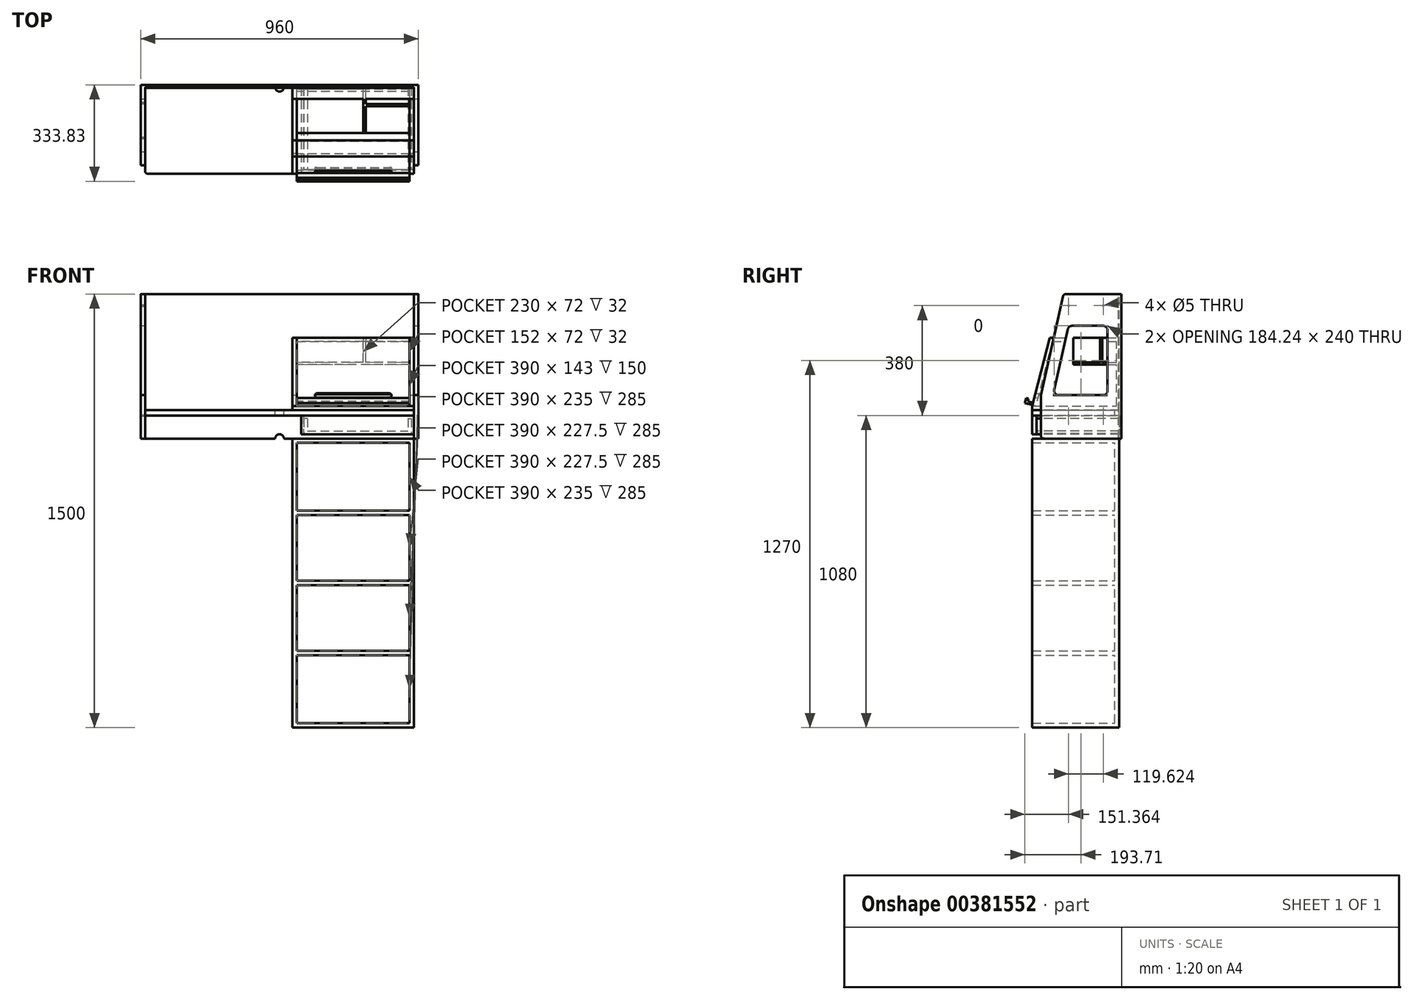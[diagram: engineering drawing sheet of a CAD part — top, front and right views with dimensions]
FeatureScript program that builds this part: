
annotation { "Feature Type Name" : "Feature", "Feature Type Description" : "" }
export const myFeature = defineFeature(function(context is Context, id is Id, definition is map)
    precondition{}
    {
        {
            var Q0;
            Q0=qCreatedBy(makeId("Front.planeOp"),FACE);
            var sketch = newSketch(context, id + "F0", { "sketchPlane" : qUnion([Q0])});
            skLineSegment(sketch, "E0.bottom", {"start": v(0, 0) * mm, "end": v(-960, 0) * mm});
            skLineSegment(sketch, "E0.top", {"start": v(0, 500) * mm, "end": v(-960, 500) * mm});
            skLineSegment(sketch, "E0.left", {"start": v(0, 0) * mm, "end": v(0, 500) * mm});
            skLineSegment(sketch, "E0.right", {"start": v(-960, 0) * mm, "end": v(-960, 500) * mm});
            skLineSegment(sketch, "E1.0", {"start": v(-945, 0) * mm, "end": v(-945, 500) * mm});
            skLineSegment(sketch, "E2.0", {"start": v(-15, 0) * mm, "end": v(-15, 500) * mm});
            skCircle(sketch, "E3", {"center": v(-480, 0) * mm, "radius": 15 * mm});
            skSolve(sketch);
        }
        {
            var Q0;
            {var subQ0=sQuery(id+"F0.wireOp",EDGE,"E0.right");Q0=makeQuery(id+"F0.imprint","IMPRINT",FACE,{"disambiguationData":[TD([[makeQuery(id+"F0.imprint","IMPRINT",EDGE,{"derivedFrom":subQ0}),-1.0]])]});}
            var Q1;
            {var subQ0=sQuery(id+"F0.wireOp",EDGE,"E1.0");Q1=makeQuery(id+"F0.imprint","IMPRINT",FACE,{"disambiguationData":[TD([[makeQuery(id+"F0.imprint","IMPRINT",EDGE,{"derivedFrom":subQ0}),-1.0]])]});}
            var Q2;
            {var subQ0=sQuery(id+"F0.wireOp",EDGE,"E0.left");Q2=makeQuery(id+"F0.imprint","IMPRINT",FACE,{"disambiguationData":[TD([[makeQuery(id+"F0.imprint","IMPRINT",EDGE,{"derivedFrom":subQ0}),1.0]])]});}
            extrude(context, id + "F1", {"entities" : qUnion([Q0, Q1, Q2]), "oppositeDirection" : true, "depth" : 8 * mm});
        }
        {
            var Q0;
            {var subQ0=sQuery(id+"F0.wireOp",EDGE,"E0.right");Q0=makeQuery(id+"F0.imprint","IMPRINT",FACE,{"disambiguationData":[TD([[makeQuery(id+"F0.imprint","IMPRINT",EDGE,{"derivedFrom":subQ0}),-1.0]])]});}
            var Q1;
            {var subQ0=sQuery(id+"F0.wireOp",EDGE,"E0.left");Q1=makeQuery(id+"F0.imprint","IMPRINT",FACE,{"disambiguationData":[TD([[makeQuery(id+"F0.imprint","IMPRINT",EDGE,{"derivedFrom":subQ0}),1.0]])]});}
            extrude(context, id + "F2", {"entities" : qUnion([Q0, Q1]), "operationType" : NewBodyOperationType.ADD, "depth" : 270 * mm});
        }
        {
            var Q0;
            {var subQ0=sQuery(id+"F0.wireOp",EDGE,"E0.top");Q0=makeQuery(id+"F2.opExtrude","CAP_EDGE",EDGE,{"disambiguationData":[OSD([subQ0]),TDD([makeQuery(id+"F0.imprint","IMPRINT",EDGE,{"disambiguationData":[TD([[makeQuery(id+"F0.imprint","INTERSECT",VERTEX,{"derivedFrom":[subQ0,sQuery(id+"F0.wireOp",EDGE,"E0.right")]}),1.0]])],"derivedFrom":subQ0})])],"isStart":false});}
            var Q1;
            {var subQ0=sQuery(id+"F0.wireOp",EDGE,"E0.top");Q1=makeQuery(id+"F2.opExtrude","CAP_EDGE",EDGE,{"disambiguationData":[OSD([subQ0]),TDD([makeQuery(id+"F0.imprint","IMPRINT",EDGE,{"disambiguationData":[TD([[makeQuery(id+"F0.imprint","INTERSECT",VERTEX,{"derivedFrom":[subQ0,sQuery(id+"F0.wireOp",EDGE,"E0.left")]}),-1.0]])],"derivedFrom":subQ0})])],"isStart":false});}
            chamfer(context, id + "F3", {"entities" : qUnion([Q0, Q1]), "chamferType" : ChamferType.TWO_OFFSETS, "width1" : 350 * mm, "oppositeDirection" : false, "width2" : 78 * mm, "tangentPropagation" : true});
        }
        {
            var Q0;
            Q0=makeQuery(id+"F2.opExtrude","SWEPT_FACE",FACE,{"disambiguationData":[OSD([sQuery(id+"F0.wireOp",EDGE,"E1.0")])]});
            var sketch = newSketch(context, id + "F4", { "sketchPlane" : qUnion([Q0])});
            skLineSegment(sketch, "E4.bottom", {"start": v(0, 80) * mm, "end": v(-270, 80) * mm});
            skLineSegment(sketch, "E4.top", {"start": v(0, 98) * mm, "end": v(-270, 98) * mm});
            skLineSegment(sketch, "E4.left", {"start": v(0, 80) * mm, "end": v(0, 98) * mm});
            skLineSegment(sketch, "E4.right", {"start": v(-270, 80) * mm, "end": v(-270, 98) * mm});
            skLineSegment(sketch, "E5", {"start": v(-174.47, 80) * mm, "end": v(-174.47, 500) * mm, "construction": true});
            skPoint(sketch, "E6", {"position": v(-174.47, 460) * mm});
            skPoint(sketch, "E7", {"position": v(-114.65, 98) * mm});
            skLineSegment(sketch, "E8", {"start": v(-114.65, 98) * mm, "end": v(-114.65, 164.65) * mm, "construction": true});
            skPoint(sketch, "E9.MirrorP", {"position": v(-54.84, 460) * mm});
            skPoint(sketch, "E10", {"position": v(-174.47, 80) * mm});
            skPoint(sketch, "E11.MirrorP", {"position": v(-54.84, 80) * mm});
            skLineSegment(sketch, "E12.bottom", {"start": v(-174.47, 390) * mm, "end": v(-40, 390) * mm});
            skLineSegment(sketch, "E12.top", {"start": v(-227.95, 150) * mm, "end": v(-40, 150) * mm});
            skLineSegment(sketch, "E12.left", {"start": v(-174.47, 390) * mm, "end": v(-227.95, 150) * mm});
            skLineSegment(sketch, "E12.right", {"start": v(-40, 390) * mm, "end": v(-40, 150) * mm});
            skLineSegment(sketch, "E13.bottom", {"start": v(-270, 98) * mm, "end": v(-300, 98) * mm});
            skLineSegment(sketch, "E13.top", {"start": v(-270, 80) * mm, "end": v(-300, 80) * mm});
            skLineSegment(sketch, "E13.left", {"start": v(-270, 98) * mm, "end": v(-270, 80) * mm});
            skLineSegment(sketch, "E13.right", {"start": v(-300, 98) * mm, "end": v(-300, 80) * mm});
            skSolve(sketch);
        }
        {
            var Q0;
            {var subQ0=sQuery(id+"F4.wireOp",EDGE,"E4.left");Q0=makeQuery(id+"F4.imprint","IMPRINT",FACE,{"disambiguationData":[TD([[makeQuery(id+"F4.imprint","IMPRINT",EDGE,{"derivedFrom":subQ0}),1.0]])]});}
            var Q1;
            {var subQ0=sQuery(id+"F4.wireOp",EDGE,"E4.right");Q1=makeQuery(id+"F4.imprint","IMPRINT",FACE,{"disambiguationData":[TD([[makeQuery(id+"F4.imprint","IMPRINT",EDGE,{"derivedFrom":subQ0}),-1.0]])]});}
            var Q2;
            Q2=makeQuery(id+"F4.imprint","IMPRINT",FACE,{"disambiguationData":[TD([[makeQuery(id+"F4.imprint","IMPRINT",EDGE,{"derivedFrom":sQuery(id+"F4.wireOp",EDGE,"E13.bottom")}),1.0]])]});
            var Q3;
            Q3=makeQuery(id+"F2.opExtrude","SWEPT_FACE",FACE,{"disambiguationData":[OSD([sQuery(id+"F0.wireOp",EDGE,"E2.0")])]});
            extrude(context, id + "F5", {"entities" : qUnion([Q0, Q1, Q2]), "endBound" : BoundingType.UP_TO_SURFACE, "endBoundEntityFace" : qUnion([Q3]), "depth" : 25 * mm});
        }
        {
            var Q0;
            Q0=makeQuery(id+"F5.opExtrude","CAP_EDGE",EDGE,{"disambiguationData":[OSD([sQuery(id+"F4.wireOp",EDGE,"E13.right")])],"isStart":true});
            var Q1;
            Q1=makeQuery(id+"F5.opExtrude","CAP_EDGE",EDGE,{"disambiguationData":[OSD([sQuery(id+"F4.wireOp",EDGE,"E13.right")])],"isStart":false});
            var Q2;
            {var subQ0=sQuery(id+"F0.wireOp",EDGE,"E0.top");var subQ1=makeQuery(id+"F0.imprint","IMPRINT",EDGE,{"disambiguationData":[TD([[makeQuery(id+"F0.imprint","INTERSECT",VERTEX,{"derivedFrom":[subQ0,sQuery(id+"F0.wireOp",EDGE,"E0.right")]}),1.0]])],"derivedFrom":subQ0});Q2=makeQuery(id+"F3.opChamfer","BLEND_EDGE",EDGE,{"blendedFrom":[makeQuery(id+"F2.opExtrude","CAP_EDGE",EDGE,{"disambiguationData":[OSD([subQ0]),TDD([subQ1])],"isStart":false}),makeQuery(id+"F2.boolean.opBoolean","MERGE",FACE,{"derivedFrom":[makeQuery(id+"F1.opExtrude","SWEPT_FACE",FACE,{"disambiguationData":[OSD([subQ0])]}),makeQuery(id+"F2.opExtrude","SWEPT_FACE",FACE,{"disambiguationData":[OSD([subQ0]),TDD([makeQuery(id+"F0.imprint","IMPRINT",EDGE,{"disambiguationData":[TD([[makeQuery(id+"F0.imprint","INTERSECT",VERTEX,{"derivedFrom":[subQ0,sQuery(id+"F0.wireOp",EDGE,"E0.left")]}),-1.0]])],"derivedFrom":subQ0})])]}),makeQuery(id+"F2.opExtrude","SWEPT_FACE",FACE,{"disambiguationData":[OSD([subQ0]),TDD([subQ1])]})]})],"blendedInto":[makeQuery(id+"F2.boolean.opBoolean","MERGE",FACE,{"derivedFrom":[makeQuery(id+"F1.opExtrude","SWEPT_FACE",FACE,{"disambiguationData":[OSD([subQ0])]}),makeQuery(id+"F2.opExtrude","SWEPT_FACE",FACE,{"disambiguationData":[OSD([subQ0]),TDD([makeQuery(id+"F0.imprint","IMPRINT",EDGE,{"disambiguationData":[TD([[makeQuery(id+"F0.imprint","INTERSECT",VERTEX,{"derivedFrom":[subQ0,sQuery(id+"F0.wireOp",EDGE,"E0.left")]}),-1.0]])],"derivedFrom":subQ0})])]}),makeQuery(id+"F2.opExtrude","SWEPT_FACE",FACE,{"disambiguationData":[OSD([subQ0]),TDD([subQ1])]})]})]});}
            var Q3;
            {var subQ0=sQuery(id+"F0.wireOp",EDGE,"E0.top");var subQ1=makeQuery(id+"F0.imprint","IMPRINT",EDGE,{"disambiguationData":[TD([[makeQuery(id+"F0.imprint","INTERSECT",VERTEX,{"derivedFrom":[subQ0,sQuery(id+"F0.wireOp",EDGE,"E0.left")]}),-1.0]])],"derivedFrom":subQ0});Q3=makeQuery(id+"F3.opChamfer","BLEND_EDGE",EDGE,{"blendedFrom":[makeQuery(id+"F2.opExtrude","CAP_EDGE",EDGE,{"disambiguationData":[OSD([subQ0]),TDD([subQ1])],"isStart":false}),makeQuery(id+"F2.boolean.opBoolean","MERGE",FACE,{"derivedFrom":[makeQuery(id+"F1.opExtrude","SWEPT_FACE",FACE,{"disambiguationData":[OSD([subQ0])]}),makeQuery(id+"F2.opExtrude","SWEPT_FACE",FACE,{"disambiguationData":[OSD([subQ0]),TDD([subQ1])]}),makeQuery(id+"F2.opExtrude","SWEPT_FACE",FACE,{"disambiguationData":[OSD([subQ0]),TDD([makeQuery(id+"F0.imprint","IMPRINT",EDGE,{"disambiguationData":[TD([[makeQuery(id+"F0.imprint","INTERSECT",VERTEX,{"derivedFrom":[subQ0,sQuery(id+"F0.wireOp",EDGE,"E0.right")]}),1.0]])],"derivedFrom":subQ0})])]})]})],"blendedInto":[makeQuery(id+"F2.boolean.opBoolean","MERGE",FACE,{"derivedFrom":[makeQuery(id+"F1.opExtrude","SWEPT_FACE",FACE,{"disambiguationData":[OSD([subQ0])]}),makeQuery(id+"F2.opExtrude","SWEPT_FACE",FACE,{"disambiguationData":[OSD([subQ0]),TDD([subQ1])]}),makeQuery(id+"F2.opExtrude","SWEPT_FACE",FACE,{"disambiguationData":[OSD([subQ0]),TDD([makeQuery(id+"F0.imprint","IMPRINT",EDGE,{"disambiguationData":[TD([[makeQuery(id+"F0.imprint","INTERSECT",VERTEX,{"derivedFrom":[subQ0,sQuery(id+"F0.wireOp",EDGE,"E0.right")]}),1.0]])],"derivedFrom":subQ0})])]})]})]});}
            var Q4;
            {var subQ0=sQuery(id+"F0.wireOp",EDGE,"E0.bottom");Q4=makeQuery(id+"F2.opExtrude","CAP_EDGE",EDGE,{"disambiguationData":[OSD([subQ0]),TDD([makeQuery(id+"F0.imprint","IMPRINT",EDGE,{"disambiguationData":[TD([[makeQuery(id+"F0.imprint","INTERSECT",VERTEX,{"derivedFrom":[subQ0,sQuery(id+"F0.wireOp",EDGE,"E0.left")]}),-1.0]])],"derivedFrom":subQ0})])],"isStart":false});}
            var Q5;
            {var subQ0=sQuery(id+"F0.wireOp",EDGE,"E0.bottom");Q5=makeQuery(id+"F2.opExtrude","CAP_EDGE",EDGE,{"disambiguationData":[OSD([subQ0]),TDD([makeQuery(id+"F0.imprint","IMPRINT",EDGE,{"disambiguationData":[TD([[makeQuery(id+"F0.imprint","INTERSECT",VERTEX,{"derivedFrom":[subQ0,sQuery(id+"F0.wireOp",EDGE,"E0.right")]}),1.0]])],"derivedFrom":subQ0})])],"isStart":false});}
            fillet(context, id + "F6", {"entities" : qUnion([Q0, Q1, Q2, Q3, Q4, Q5]), "radius" : 10 * mm, "tangentPropagation" : true, "allowEdgeOverflow" : false});
        }
        {
            var Q0;
            Q0=qCreatedBy(makeId("Front.planeOp"),FACE);
            var sketch = newSketch(context, id + "F7", { "sketchPlane" : qUnion([Q0])});
            skLineSegment(sketch, "E14.bottom", {"start": v(-15, 98) * mm, "end": v(-435, 98) * mm});
            skLineSegment(sketch, "E14.top", {"start": v(-15, 348) * mm, "end": v(-435, 348) * mm});
            skLineSegment(sketch, "E14.left", {"start": v(-15, 98) * mm, "end": v(-15, 348) * mm});
            skLineSegment(sketch, "E14.right", {"start": v(-435, 98) * mm, "end": v(-435, 348) * mm});
            skLineSegment(sketch, "E15.0", {"start": v(-420, 95) * mm, "end": v(-420, 348) * mm});
            skLineSegment(sketch, "E16.0", {"start": v(-30, 98) * mm, "end": v(-30, 348) * mm});
            skLineSegment(sketch, "E17.0", {"start": v(-15, 113) * mm, "end": v(-435, 113) * mm});
            skSolve(sketch);
        }
        {
            var Q0;
            {var subQ0=sQuery(id+"F7.wireOp",EDGE,"E14.right");var subQ1=sQuery(id+"F7.wireOp",EDGE,"E14.top");var subQ2=makeQuery(id+"F7.imprint","INTERSECT",VERTEX,{"derivedFrom":[subQ1,subQ0]});Q0=makeQuery(id+"F7.imprint","IMPRINT",FACE,{"disambiguationData":[TD([[makeQuery(id+"F7.imprint","IMPRINT",EDGE,{"disambiguationData":[TD([[subQ2,1.0]])],"derivedFrom":subQ1}),1.0]])]});}
            var Q1;
            {var subQ0=sQuery(id+"F7.wireOp",EDGE,"E14.right");var subQ1=sQuery(id+"F7.wireOp",EDGE,"E14.bottom");var subQ2=makeQuery(id+"F7.imprint","INTERSECT",VERTEX,{"derivedFrom":[subQ1,subQ0]});Q1=makeQuery(id+"F7.imprint","IMPRINT",FACE,{"disambiguationData":[TD([[makeQuery(id+"F7.imprint","IMPRINT",EDGE,{"disambiguationData":[TD([[subQ2,1.0]])],"derivedFrom":subQ1}),-1.0]])]});}
            var Q2;
            {var subQ0=sQuery(id+"F7.wireOp",EDGE,"E14.left");var subQ1=sQuery(id+"F7.wireOp",EDGE,"E14.top");var subQ2=makeQuery(id+"F7.imprint","INTERSECT",VERTEX,{"derivedFrom":[subQ1,subQ0]});Q2=makeQuery(id+"F7.imprint","IMPRINT",FACE,{"disambiguationData":[TD([[makeQuery(id+"F7.imprint","IMPRINT",EDGE,{"disambiguationData":[TD([[subQ2,-1.0]])],"derivedFrom":subQ1}),1.0]])]});}
            var Q3;
            {var subQ0=sQuery(id+"F7.wireOp",EDGE,"E14.left");var subQ1=sQuery(id+"F7.wireOp",EDGE,"E14.bottom");var subQ2=makeQuery(id+"F7.imprint","INTERSECT",VERTEX,{"derivedFrom":[subQ1,subQ0]});Q3=makeQuery(id+"F7.imprint","IMPRINT",FACE,{"disambiguationData":[TD([[makeQuery(id+"F7.imprint","IMPRINT",EDGE,{"disambiguationData":[TD([[subQ2,-1.0]])],"derivedFrom":subQ1}),-1.0]])]});}
            var Q4;
            {var subQ0=sQuery(id+"F7.wireOp",EDGE,"E15.0");var subQ1=sQuery(id+"F7.wireOp",EDGE,"E14.bottom");var subQ2=makeQuery(id+"F7.imprint","INTERSECT",VERTEX,{"derivedFrom":[subQ1,subQ0]});Q4=makeQuery(id+"F7.imprint","IMPRINT",FACE,{"disambiguationData":[TD([[makeQuery(id+"F7.imprint","IMPRINT",EDGE,{"disambiguationData":[TD([[subQ2,1.0]])],"derivedFrom":subQ1}),-1.0]])]});}
            extrude(context, id + "F8", {"entities" : qUnion([Q0, Q1, Q2, Q3, Q4]), "depth" : 300 * mm});
        }
        {
            var Q0;
            {var subQ0=sQuery(id+"F7.wireOp",EDGE,"E15.0");var subQ1=sQuery(id+"F7.wireOp",EDGE,"E14.top");var subQ2=makeQuery(id+"F7.imprint","INTERSECT",VERTEX,{"derivedFrom":[subQ1,subQ0]});Q0=makeQuery(id+"F7.imprint","IMPRINT",FACE,{"disambiguationData":[TD([[makeQuery(id+"F7.imprint","IMPRINT",EDGE,{"disambiguationData":[TD([[subQ2,1.0]])],"derivedFrom":subQ1}),1.0]])]});}
            extrude(context, id + "F9", {"entities" : qUnion([Q0]), "depth" : 8 * mm});
        }
        {
            var Q0;
            {var subQ0=sQuery(id+"F7.wireOp",EDGE,"E14.top");Q0=makeQuery(id+"F8.opExtrude","CAP_EDGE",EDGE,{"disambiguationData":[OSD([subQ0]),TDD([makeQuery(id+"F7.imprint","IMPRINT",EDGE,{"disambiguationData":[TD([[makeQuery(id+"F7.imprint","INTERSECT",VERTEX,{"derivedFrom":[subQ0,sQuery(id+"F7.wireOp",EDGE,"E14.right")]}),1.0]])],"derivedFrom":subQ0})])],"isStart":false});}
            var Q1;
            {var subQ0=sQuery(id+"F7.wireOp",EDGE,"E14.top");Q1=makeQuery(id+"F8.opExtrude","CAP_EDGE",EDGE,{"disambiguationData":[OSD([subQ0]),TDD([makeQuery(id+"F7.imprint","IMPRINT",EDGE,{"disambiguationData":[TD([[makeQuery(id+"F7.imprint","INTERSECT",VERTEX,{"derivedFrom":[subQ0,sQuery(id+"F7.wireOp",EDGE,"E14.left")]}),-1.0]])],"derivedFrom":subQ0})])],"isStart":false});}
            chamfer(context, id + "F10", {"entities" : qUnion([Q0, Q1]), "chamferType" : ChamferType.TWO_OFFSETS, "width1" : 235 * mm, "oppositeDirection" : false, "width2" : 60 * mm, "tangentPropagation" : true});
        }
        {
            var Q0;
            Q0=makeQuery(id+"F8.opExtrude","SWEPT_FACE",FACE,{"disambiguationData":[OSD([sQuery(id+"F7.wireOp",EDGE,"E15.0")])]});
            var sketch = newSketch(context, id + "F11", { "sketchPlane" : qUnion([Q0])});
            skLineSegment(sketch, "E18", {"start": v(-240, 348) * mm, "end": v(-299.24, 115.97) * mm});
            skLineSegment(sketch, "E19", {"start": v(-299.24, 115.97) * mm, "end": v(-287.62, 113) * mm});
            skLineSegment(sketch, "E20", {"start": v(-287.62, 113) * mm, "end": v(-227.62, 348) * mm});
            skLineSegment(sketch, "E21", {"start": v(-227.62, 348) * mm, "end": v(-240, 348) * mm});
            skLineSegment(sketch, "E22.0", {"start": v(-243.06, 336) * mm, "end": v(0, 336) * mm});
            skLineSegment(sketch, "E23", {"start": v(-299.24, 115.97) * mm, "end": v(-325.83, 122.76) * mm});
            skLineSegment(sketch, "E24", {"start": v(-325.83, 122.76) * mm, "end": v(-321.38, 140.2) * mm});
            skLineSegment(sketch, "E25", {"start": v(-321.38, 140.2) * mm, "end": v(-313.63, 138.22) * mm});
            skLineSegment(sketch, "E26", {"start": v(-313.63, 138.22) * mm, "end": v(-316.1, 128.53) * mm});
            skLineSegment(sketch, "E27", {"start": v(-316.1, 128.53) * mm, "end": v(-297.26, 123.72) * mm});
            skPoint(sketch, "E28", {"position": v(-158, 336) * mm});
            skPoint(sketch, "E28.positionSnap0", {"position": v(-158, 348) * mm});
            skLineSegment(sketch, "E29", {"start": v(-158, 348) * mm, "end": v(-158, 336) * mm});
            skLineSegment(sketch, "E30.bottom", {"start": v(-158, 256) * mm, "end": v(-8, 256) * mm});
            skLineSegment(sketch, "E30.top", {"start": v(-158, 264) * mm, "end": v(-8, 264) * mm});
            skLineSegment(sketch, "E30.left", {"start": v(-158, 264) * mm, "end": v(-158, 256) * mm});
            skLineSegment(sketch, "E30.right", {"start": v(-8, 264) * mm, "end": v(-8, 256) * mm});
            skSolve(sketch);
        }
        {
            var Q0;
            {var subQ1=sQuery(id+"F7.wireOp",EDGE,"E15.0");var subQ4=sQuery(id+"F11.wireOp",EDGE,"E22.0");var subQ6=makeQuery(id+"F8.opExtrude","CAP_EDGE",EDGE,{"disambiguationData":[OSD([subQ1])],"isStart":true});var subQ8=makeQuery(id+"F11.imprint","INTERSECT",VERTEX,{"derivedFrom":[subQ6,subQ4]});Q0=makeQuery(id+"F11.imprint","IMPRINT",FACE,{"disambiguationData":[TD([[makeQuery(id+"F11.imprint","IMPRINT",EDGE,{"disambiguationData":[TD([[subQ8,1.0]])],"derivedFrom":subQ4}),1.0]])]});}
            var Q1;
            {var subQ0=sQuery(id+"F11.wireOp",EDGE,"E21");Q1=makeQuery(id+"F11.imprint","IMPRINT",FACE,{"disambiguationData":[TD([[makeQuery(id+"F11.imprint","IMPRINT",EDGE,{"derivedFrom":subQ0}),-1.0]])]});}
            var Q2;
            {var subQ0=sQuery(id+"F11.wireOp",EDGE,"E19");Q2=makeQuery(id+"F11.imprint","IMPRINT",FACE,{"disambiguationData":[TD([[makeQuery(id+"F11.imprint","IMPRINT",EDGE,{"derivedFrom":subQ0}),1.0]])]});}
            var Q3;
            {var subQ0=sQuery(id+"F11.wireOp",EDGE,"E23");Q3=makeQuery(id+"F11.imprint","IMPRINT",FACE,{"disambiguationData":[TD([[makeQuery(id+"F11.imprint","IMPRINT",EDGE,{"derivedFrom":subQ0}),-1.0]])]});}
            var Q4;
            {var subQ5=sQuery(id+"F11.wireOp",EDGE,"Vka6C3qe-eKzw-OUEN-JvXl-aBNwLwRMFBuR");Q4=makeQuery(id+"F11.imprint","IMPRINT",FACE,{"disambiguationData":[TD([[makeQuery(id+"F11.imprint","IMPRINT",EDGE,{"derivedFrom":subQ5}),-1.0]])]});}
            var Q5;
            {var subQ5=sQuery(id+"F11.wireOp",EDGE,"E29");Q5=makeQuery(id+"F11.imprint","IMPRINT",FACE,{"disambiguationData":[TD([[makeQuery(id+"F11.imprint","IMPRINT",EDGE,{"derivedFrom":subQ5}),-1.0]])]});}
            var Q6;
            Q6=makeQuery(id+"F8.opExtrude","SWEPT_FACE",FACE,{"disambiguationData":[OSD([sQuery(id+"F7.wireOp",EDGE,"E16.0")])]});
            extrude(context, id + "F12", {"entities" : qUnion([Q0, Q1, Q2, Q3, Q4, Q5]), "endBound" : BoundingType.UP_TO_SURFACE, "endBoundEntityFace" : qUnion([Q6]), "depth" : 25 * mm});
        }
        {
            var Q0;
            Q0=makeQuery(id+"F12.opExtrude","SWEPT_FACE",FACE,{"disambiguationData":[OSD([sQuery(id+"F11.wireOp",EDGE,"E18")])]});
            var sketch = newSketch(context, id + "F13", { "sketchPlane" : qUnion([Q0])});
            skLineSegment(sketch, "E31.bottom", {"start": v(-350, 80.12) * mm, "end": v(-100, 80.12) * mm});
            skLineSegment(sketch, "E31.top", {"start": v(-350, 65.12) * mm, "end": v(-100, 65.12) * mm});
            skLineSegment(sketch, "E31.left", {"start": v(-350, 80.12) * mm, "end": v(-350, 65.12) * mm});
            skLineSegment(sketch, "E31.right", {"start": v(-100, 80.12) * mm, "end": v(-100, 65.12) * mm});
            skPoint(sketch, "E32", {"position": v(-225, 80.12) * mm});
            skArc(sketch, "E33", {"start": v(-350, 80.12) * mm, "mid": v(-357.5, 72.62) * mm, "end": v(-350, 65.12) * mm});
            skArc(sketch, "E34", {"start": v(-100, 65.12) * mm, "mid": v(-92.5, 72.62) * mm, "end": v(-100, 80.12) * mm});
            skSolve(sketch);
        }
        {
            var Q0;
            Q0=makeQuery(id+"F13.imprint","IMPRINT",FACE,{"disambiguationData":[TD([[makeQuery(id+"F13.imprint","IMPRINT",EDGE,{"derivedFrom":sQuery(id+"F13.wireOp",EDGE,"E31.bottom")}),-1.0]])]});
            var Q1;
            Q1=makeQuery(id+"F13.imprint","IMPRINT",FACE,{"disambiguationData":[TD([[makeQuery(id+"F13.imprint","IMPRINT",EDGE,{"derivedFrom":sQuery(id+"F13.wireOp",EDGE,"E31.left")}),-1.0]])]});
            var Q2;
            Q2=makeQuery(id+"F13.imprint","IMPRINT",FACE,{"disambiguationData":[TD([[makeQuery(id+"F13.imprint","IMPRINT",EDGE,{"derivedFrom":sQuery(id+"F13.wireOp",EDGE,"E31.right")}),1.0]])]});
            extrude(context, id + "F14", {"entities" : qUnion([Q0, Q1, Q2]), "operationType" : NewBodyOperationType.REMOVE, "oppositeDirection" : true, "depth" : 25 * mm});
        }
        {
            var Q0;
            {var subQ4=sQuery(id+"F11.wireOp",EDGE,"E29");Q0=makeQuery(id+"F11.imprint","IMPRINT",FACE,{"disambiguationData":[TD([[makeQuery(id+"F11.imprint","IMPRINT",EDGE,{"derivedFrom":subQ4}),1.0]])]});}
            var Q1;
            Q1=makeQuery(id+"F8.opExtrude","SWEPT_FACE",FACE,{"disambiguationData":[OSD([sQuery(id+"F7.wireOp",EDGE,"E16.0")])]});
            extrude(context, id + "F15", {"entities" : qUnion([Q0]), "endBound" : BoundingType.UP_TO_SURFACE, "endBoundEntityFace" : qUnion([Q1]), "depth" : 25 * mm});
        }
        {
            var Q0;
            Q0=makeQuery(id+"F15.opExtrude","SWEPT_BODY",BODY,{"disambiguationData":[OSD([sQuery(id+"F7.wireOp",EDGE,"E14.top"),sQuery(id+"F7.wireOp",EDGE,"E15.0"),sQuery(id+"F11.wireOp",EDGE,"E22.0"),sQuery(id+"F11.wireOp",EDGE,"E29")])]});
            var Q1;
            Q1=makeQuery(id+"F12.opExtrude","SWEPT_BODY",BODY,{"disambiguationData":[OSD([sQuery(id+"F7.wireOp",EDGE,"E14.top"),sQuery(id+"F7.wireOp",EDGE,"E15.0"),sQuery(id+"F11.wireOp",EDGE,"E18"),sQuery(id+"F11.wireOp",EDGE,"E19"),sQuery(id+"F11.wireOp",EDGE,"E20"),sQuery(id+"F11.wireOp",EDGE,"E21"),sQuery(id+"F11.wireOp",EDGE,"E22.0"),sQuery(id+"F11.wireOp",EDGE,"E23"),sQuery(id+"F11.wireOp",EDGE,"E24"),sQuery(id+"F11.wireOp",EDGE,"E25"),sQuery(id+"F11.wireOp",EDGE,"E26"),sQuery(id+"F11.wireOp",EDGE,"E27")])]});
            booleanBodies(context, id + "F16", {"operationType" : BooleanOperationType.SUBTRACTION, "tools" : qUnion([Q0]), "targets" : qUnion([Q1]), "keepTools" : true});
        }
        {
            var Q0;
            Q0=makeQuery(id+"F5.opExtrude","SWEPT_FACE",FACE,{"disambiguationData":[OSD([sQuery(id+"F4.wireOp",EDGE,"E13.right")])]});
            var sketch = newSketch(context, id + "F17", { "sketchPlane" : qUnion([Q0])});
            skLineSegment(sketch, "E35.bottom", {"start": v(-15, 80) * mm, "end": v(-405, 80) * mm});
            skLineSegment(sketch, "E35.top", {"start": v(-15, 15) * mm, "end": v(-405, 15) * mm});
            skLineSegment(sketch, "E35.left", {"start": v(-15, 80) * mm, "end": v(-15, 15) * mm});
            skLineSegment(sketch, "E35.right", {"start": v(-405, 80) * mm, "end": v(-405, 15) * mm});
            skLineSegment(sketch, "E36.bottom", {"start": v(-405, 15) * mm, "end": v(-420, 15) * mm});
            skLineSegment(sketch, "E36.top", {"start": v(-405, 80) * mm, "end": v(-420, 80) * mm});
            skLineSegment(sketch, "E36.left", {"start": v(-405, 15) * mm, "end": v(-405, 80) * mm});
            skLineSegment(sketch, "E36.right", {"start": v(-420, 15) * mm, "end": v(-420, 80) * mm});
            skSolve(sketch);
        }
        {
            var Q0;
            Q0=makeQuery(id+"F17.imprint","IMPRINT",FACE,{"disambiguationData":[TD([[makeQuery(id+"F17.imprint","IMPRINT",EDGE,{"derivedFrom":sQuery(id+"F17.wireOp",EDGE,"E35.bottom")}),1.0]])]});
            extrude(context, id + "F18", {"entities" : qUnion([Q0]), "oppositeDirection" : true, "depth" : 15 * mm});
        }
        {
            var Q0;
            Q0=makeQuery(id+"F18.opExtrude","CAP_FACE",FACE,{"disambiguationData":[OSD([sQuery(id+"F17.wireOp",EDGE,"E35.bottom"),sQuery(id+"F17.wireOp",EDGE,"E35.top"),sQuery(id+"F17.wireOp",EDGE,"E35.left"),sQuery(id+"F17.wireOp",EDGE,"E35.right")])],"isStart":false});
            var sketch = newSketch(context, id + "F19", { "sketchPlane" : qUnion([Q0])});
            skLineSegment(sketch, "E37.bottom", {"start": v(24, 15) * mm, "end": v(36, 15) * mm});
            skLineSegment(sketch, "E37.top", {"start": v(24, 68.96) * mm, "end": v(36, 68.96) * mm});
            skLineSegment(sketch, "E37.left", {"start": v(24, 15) * mm, "end": v(24, 68.96) * mm});
            skLineSegment(sketch, "E37.right", {"start": v(36, 15) * mm, "end": v(36, 68.96) * mm});
            skLineSegment(sketch, "E38.bottom", {"start": v(396, 15) * mm, "end": v(384, 15) * mm});
            skLineSegment(sketch, "E38.top", {"start": v(396, 68.96) * mm, "end": v(384, 68.96) * mm});
            skLineSegment(sketch, "E38.left", {"start": v(396, 15) * mm, "end": v(396, 68.96) * mm});
            skLineSegment(sketch, "E38.right", {"start": v(384, 15) * mm, "end": v(384, 68.96) * mm});
            skLineSegment(sketch, "E39.bottom", {"start": v(36, 25.56) * mm, "end": v(384, 25.56) * mm});
            skLineSegment(sketch, "E39.top", {"start": v(36, 17.56) * mm, "end": v(384, 17.56) * mm});
            skLineSegment(sketch, "E39.left", {"start": v(36, 25.56) * mm, "end": v(36, 17.56) * mm});
            skLineSegment(sketch, "E39.right", {"start": v(384, 25.56) * mm, "end": v(384, 17.56) * mm});
            skLineSegment(sketch, "E40.bottom", {"start": v(405, 15) * mm, "end": v(397, 15) * mm});
            skLineSegment(sketch, "E40.top", {"start": v(405, 80) * mm, "end": v(397, 80) * mm});
            skLineSegment(sketch, "E40.left", {"start": v(405, 15) * mm, "end": v(405, 80) * mm});
            skLineSegment(sketch, "E40.right", {"start": v(397, 15) * mm, "end": v(397, 80) * mm});
            skSolve(sketch);
        }
        {
            var Q0;
            {var subQ1=sQuery(id+"F19.wireOp",EDGE,"E37.bottom");Q0=makeQuery(id+"F19.imprint","IMPRINT",FACE,{"disambiguationData":[TD([[makeQuery(id+"F19.imprint","IMPRINT",EDGE,{"derivedFrom":subQ1}),1.0]])]});}
            var Q1;
            Q1=makeQuery(id+"F19.imprint","IMPRINT",FACE,{"disambiguationData":[TD([[makeQuery(id+"F19.imprint","IMPRINT",EDGE,{"derivedFrom":sQuery(id+"F19.wireOp",EDGE,"E39.bottom")}),-1.0]])]});
            var Q2;
            {var subQ1=sQuery(id+"F19.wireOp",EDGE,"E38.bottom");Q2=makeQuery(id+"F19.imprint","IMPRINT",FACE,{"disambiguationData":[TD([[makeQuery(id+"F19.imprint","IMPRINT",EDGE,{"derivedFrom":subQ1}),1.0]])]});}
            var Q3;
            Q3=makeQuery(id+"F5.opExtrude","SWEPT_FACE",FACE,{"disambiguationData":[OSD([sQuery(id+"F4.wireOp",EDGE,"E4.left")])]});
            extrude(context, id + "F20", {"entities" : qUnion([Q0, Q1, Q2]), "endBound" : BoundingType.UP_TO_SURFACE, "endBoundEntityFace" : qUnion([Q3]), "depth" : 25 * mm});
        }
        {
            var Q0;
            Q0=makeQuery(id+"F19.imprint","IMPRINT",FACE,{"disambiguationData":[TD([[makeQuery(id+"F19.imprint","IMPRINT",EDGE,{"derivedFrom":sQuery(id+"F19.wireOp",EDGE,"E40.bottom")}),1.0]])]});
            var Q1;
            Q1=makeQuery(id+"F1.opExtrude","CAP_FACE",FACE,{"disambiguationData":[OSD([sQuery(id+"F0.wireOp",EDGE,"E0.bottom"),sQuery(id+"F0.wireOp",EDGE,"E0.top"),sQuery(id+"F0.wireOp",EDGE,"E0.left"),sQuery(id+"F0.wireOp",EDGE,"E0.right"),sQuery(id+"F0.wireOp",EDGE,"E3")])],"isStart":true});
            extrude(context, id + "F21", {"entities" : qUnion([Q0]), "endBound" : BoundingType.UP_TO_SURFACE, "endBoundEntityFace" : qUnion([Q1]), "depth" : 25 * mm});
        }
        {
            var Q0;
            Q0=sQuery(id+"F4.wireOp",VERTEX,"E6");
            var Q1;
            Q1=sQuery(id+"F4.wireOp",VERTEX,"E9.MirrorP");
            var Q2;
            Q2=sQuery(id+"F4.wireOp",VERTEX,"E10");
            var Q3;
            Q3=sQuery(id+"F4.wireOp",VERTEX,"E11.MirrorP");
            var Q4;
            Q4=makeQuery(id+"F1.opExtrude","SWEPT_BODY",BODY,{"disambiguationData":[OSD([sQuery(id+"F0.wireOp",EDGE,"E0.bottom"),sQuery(id+"F0.wireOp",EDGE,"E0.top"),sQuery(id+"F0.wireOp",EDGE,"E0.left"),sQuery(id+"F0.wireOp",EDGE,"E0.right"),sQuery(id+"F0.wireOp",EDGE,"E3")])]});
            hole(context, id + "F22", {"style" : HoleStyle.SIMPLE, "endStyle" : HoleEndStyle.BLIND, "holeDiameter" : 5 * mm, "holeDepth" : 12 * mm, "isTappedThrough" : true, "tappedDepth" : 12 * mm, "tapClearance" : 3, "locations" : qUnion([Q0, Q1, Q2, Q3]), "scope" : qUnion([Q4])});
        }
        {
            var Q0;
            Q0=makeQuery(id+"F4.imprint","IMPRINT",FACE,{"disambiguationData":[TD([[makeQuery(id+"F4.imprint","IMPRINT",EDGE,{"derivedFrom":sQuery(id+"F4.wireOp",EDGE,"E12.bottom")}),-1.0]])]});
            var Q1;
            {var subQ0=sQuery(id+"F0.wireOp",EDGE,"E0.left");Q1=makeQuery(id+"F2.boolean.opBoolean","MERGE",FACE,{"derivedFrom":[makeQuery(id+"F1.opExtrude","SWEPT_FACE",FACE,{"disambiguationData":[OSD([subQ0])]}),makeQuery(id+"F2.opExtrude","SWEPT_FACE",FACE,{"disambiguationData":[OSD([subQ0])]})]});}
            extrude(context, id + "F23", {"entities" : qUnion([Q0]), "operationType" : NewBodyOperationType.REMOVE, "oppositeDirection" : true, "depth" : 25 * mm, "hasSecondDirection" : true, "secondDirectionBound" : SecondDirectionBoundingType.UP_TO_SURFACE, "secondDirectionOppositeDirection" : false, "secondDirectionBoundEntityFace" : qUnion([Q1]), "secondDirectionDepth" : 25 * mm});
        }
        {
            var Q0;
            {var subQ0=sQuery(id+"F4.wireOp",EDGE,"E12.top");var subQ1=sQuery(id+"F0.wireOp",EDGE,"E0.right");var subQ2=sQuery(id+"F4.wireOp",EDGE,"E12.right");Q0=makeQuery(id+"F23.boolean.opBoolean","COPY",EDGE,{"disambiguationData":[TD([makeQuery(id+"F1.opExtrude","SWEPT_FACE",FACE,{"disambiguationData":[OSD([subQ1])]})])],"derivedFrom":makeQuery(id+"F23.opExtrude","SWEPT_EDGE",EDGE,{"disambiguationData":[OSD([subQ0,subQ2])]})});}
            var Q1;
            {var subQ0=sQuery(id+"F4.wireOp",EDGE,"E12.top");var subQ1=sQuery(id+"F0.wireOp",EDGE,"E0.right");var subQ2=sQuery(id+"F4.wireOp",EDGE,"E12.left");Q1=makeQuery(id+"F23.boolean.opBoolean","COPY",EDGE,{"disambiguationData":[TD([makeQuery(id+"F1.opExtrude","SWEPT_FACE",FACE,{"disambiguationData":[OSD([subQ1])]})])],"derivedFrom":makeQuery(id+"F23.opExtrude","SWEPT_EDGE",EDGE,{"disambiguationData":[OSD([subQ0,subQ2])]})});}
            var Q2;
            {var subQ0=sQuery(id+"F4.wireOp",EDGE,"E12.bottom");var subQ1=sQuery(id+"F0.wireOp",EDGE,"E0.right");var subQ2=sQuery(id+"F4.wireOp",EDGE,"E12.right");Q2=makeQuery(id+"F23.boolean.opBoolean","COPY",EDGE,{"disambiguationData":[TD([makeQuery(id+"F1.opExtrude","SWEPT_FACE",FACE,{"disambiguationData":[OSD([subQ1])]})])],"derivedFrom":makeQuery(id+"F23.opExtrude","SWEPT_EDGE",EDGE,{"disambiguationData":[OSD([subQ0,subQ2])]})});}
            var Q3;
            {var subQ0=sQuery(id+"F4.wireOp",EDGE,"E12.top");var subQ1=sQuery(id+"F0.wireOp",EDGE,"E0.left");var subQ2=sQuery(id+"F4.wireOp",EDGE,"E12.left");Q3=makeQuery(id+"F23.boolean.opBoolean","COPY",EDGE,{"disambiguationData":[TD([makeQuery(id+"F1.opExtrude","SWEPT_FACE",FACE,{"disambiguationData":[OSD([subQ1])]})])],"derivedFrom":makeQuery(id+"F23.opExtrude","SWEPT_EDGE",EDGE,{"disambiguationData":[OSD([subQ0,subQ2])]})});}
            var Q4;
            {var subQ0=sQuery(id+"F4.wireOp",EDGE,"E12.top");var subQ1=sQuery(id+"F0.wireOp",EDGE,"E0.left");var subQ2=sQuery(id+"F4.wireOp",EDGE,"E12.right");Q4=makeQuery(id+"F23.boolean.opBoolean","COPY",EDGE,{"disambiguationData":[TD([makeQuery(id+"F1.opExtrude","SWEPT_FACE",FACE,{"disambiguationData":[OSD([subQ1])]})])],"derivedFrom":makeQuery(id+"F23.opExtrude","SWEPT_EDGE",EDGE,{"disambiguationData":[OSD([subQ0,subQ2])]})});}
            var Q5;
            {var subQ0=sQuery(id+"F0.wireOp",EDGE,"E0.left");var subQ1=sQuery(id+"F4.wireOp",EDGE,"E12.bottom");var subQ2=sQuery(id+"F4.wireOp",EDGE,"E12.right");Q5=makeQuery(id+"F23.boolean.opBoolean","COPY",EDGE,{"disambiguationData":[TD([makeQuery(id+"F1.opExtrude","SWEPT_FACE",FACE,{"disambiguationData":[OSD([subQ0])]})])],"derivedFrom":makeQuery(id+"F23.opExtrude","SWEPT_EDGE",EDGE,{"disambiguationData":[OSD([subQ1,subQ2])]})});}
            var Q6;
            {var subQ0=sQuery(id+"F0.wireOp",EDGE,"E0.left");var subQ1=sQuery(id+"F4.wireOp",EDGE,"E12.bottom");var subQ2=sQuery(id+"F4.wireOp",EDGE,"E12.left");Q6=makeQuery(id+"F23.boolean.opBoolean","COPY",EDGE,{"disambiguationData":[TD([makeQuery(id+"F1.opExtrude","SWEPT_FACE",FACE,{"disambiguationData":[OSD([subQ0])]})])],"derivedFrom":makeQuery(id+"F23.opExtrude","SWEPT_EDGE",EDGE,{"disambiguationData":[OSD([subQ1,subQ2])]})});}
            var Q7;
            {var subQ0=sQuery(id+"F4.wireOp",EDGE,"E12.bottom");var subQ1=sQuery(id+"F0.wireOp",EDGE,"E0.right");var subQ2=sQuery(id+"F4.wireOp",EDGE,"E12.left");Q7=makeQuery(id+"F23.boolean.opBoolean","COPY",EDGE,{"disambiguationData":[TD([makeQuery(id+"F1.opExtrude","SWEPT_FACE",FACE,{"disambiguationData":[OSD([subQ1])]})])],"derivedFrom":makeQuery(id+"F23.opExtrude","SWEPT_EDGE",EDGE,{"disambiguationData":[OSD([subQ0,subQ2])]})});}
            fillet(context, id + "F24", {"entities" : qUnion([Q0, Q1, Q2, Q3, Q4, Q5, Q6, Q7]), "radius" : 15 * mm, "tangentPropagation" : true, "allowEdgeOverflow" : false});
        }
        {
            var Q0;
            Q0=makeQuery(id+"F5.opExtrude","SWEPT_FACE",FACE,{"disambiguationData":[OSD([sQuery(id+"F4.wireOp",EDGE,"E4.top"),sQuery(id+"F4.wireOp",EDGE,"E13.bottom")])]});
            var sketch = newSketch(context, id + "F25", { "sketchPlane" : qUnion([Q0])});
            skCircle(sketch, "E41", {"center": v(-480, 0) * mm, "radius": 15 * mm});
            skSolve(sketch);
        }
        {
            var Q0;
            {var subQ0=sQuery(id+"F25.wireOp",EDGE,"E41");var subQ1=makeQuery(id+"F5.opExtrude","SWEPT_EDGE",EDGE,{"disambiguationData":[OSD([sQuery(id+"F0.wireOp",EDGE,"E1.0"),sQuery(id+"F4.wireOp",EDGE,"E4.top"),sQuery(id+"F4.wireOp",EDGE,"E4.left")])]});var subQ2=makeQuery(id+"F25.imprint","INTERSECT",VERTEX,{"disambiguationData":[OD(0.0)],"derivedFrom":[subQ1,subQ0]});Q0=makeQuery(id+"F25.imprint","IMPRINT",FACE,{"disambiguationData":[TD([[makeQuery(id+"F25.imprint","IMPRINT",EDGE,{"disambiguationData":[TD([[subQ2,-1.0]])],"derivedFrom":subQ0}),1.0]])]});}
            extrude(context, id + "F26", {"entities" : qUnion([Q0]), "operationType" : NewBodyOperationType.REMOVE, "oppositeDirection" : true, "depth" : 25 * mm});
        }
        {
            var Q0;
            {var subQ0=sQuery(id+"F7.wireOp",EDGE,"E14.top");Q0=makeQuery(id+"F8.opExtrude","SWEPT_FACE",FACE,{"disambiguationData":[OSD([subQ0]),TDD([makeQuery(id+"F7.imprint","IMPRINT",EDGE,{"disambiguationData":[TD([[makeQuery(id+"F7.imprint","INTERSECT",VERTEX,{"derivedFrom":[subQ0,sQuery(id+"F7.wireOp",EDGE,"E14.right")]}),1.0]])],"derivedFrom":subQ0})])]});}
            var sketch = newSketch(context, id + "F27", { "sketchPlane" : qUnion([Q0])});
            skLineSegment(sketch, "E42.bottom", {"start": v(-420, -8) * mm, "end": v(-190, -8) * mm});
            skLineSegment(sketch, "E42.top", {"start": v(-420, -158) * mm, "end": v(-190, -158) * mm});
            skLineSegment(sketch, "E42.left", {"start": v(-420, -8) * mm, "end": v(-420, -158) * mm});
            skLineSegment(sketch, "E42.right", {"start": v(-190, -8) * mm, "end": v(-190, -158) * mm});
            skLineSegment(sketch, "E43.bottom", {"start": v(-190, -8) * mm, "end": v(-182, -8) * mm});
            skLineSegment(sketch, "E43.top", {"start": v(-190, -158) * mm, "end": v(-182, -158) * mm});
            skLineSegment(sketch, "E43.right", {"start": v(-182, -8) * mm, "end": v(-182, -158) * mm});
            skLineSegment(sketch, "E44.bottom", {"start": v(-182, -58) * mm, "end": v(-30, -58) * mm});
            skLineSegment(sketch, "E44.top", {"start": v(-182, -66) * mm, "end": v(-30, -66) * mm});
            skLineSegment(sketch, "E44.left", {"start": v(-182, -58) * mm, "end": v(-182, -66) * mm});
            skLineSegment(sketch, "E44.right", {"start": v(-30, -58) * mm, "end": v(-30, -66) * mm});
            skSolve(sketch);
        }
        {
            var Q0;
            Q0=makeQuery(id+"F11.imprint","IMPRINT",FACE,{"disambiguationData":[TD([[makeQuery(id+"F11.imprint","IMPRINT",EDGE,{"derivedFrom":sQuery(id+"F11.wireOp",EDGE,"E30.bottom")}),1.0]])]});
            var Q1;
            Q1=makeQuery(id+"F8.opExtrude","SWEPT_FACE",FACE,{"disambiguationData":[OSD([sQuery(id+"F7.wireOp",EDGE,"E16.0")])]});
            extrude(context, id + "F28", {"entities" : qUnion([Q0]), "operationType" : NewBodyOperationType.ADD, "endBound" : BoundingType.UP_TO_SURFACE, "endBoundEntityFace" : qUnion([Q1]), "depth" : 25 * mm});
        }
        {
            var Q0;
            {var subQ1=sQuery(id+"F27.wireOp",EDGE,"E43.bottom");Q0=makeQuery(id+"F27.imprint","IMPRINT",FACE,{"disambiguationData":[TD([[makeQuery(id+"F27.imprint","IMPRINT",EDGE,{"derivedFrom":subQ1}),-1.0]])]});}
            var Q1;
            Q1=makeQuery(id+"F27.imprint","IMPRINT",FACE,{"disambiguationData":[TD([[makeQuery(id+"F27.imprint","IMPRINT",EDGE,{"derivedFrom":sQuery(id+"F27.wireOp",EDGE,"E44.bottom")}),-1.0]])]});
            var Q2;
            Q2=makeQuery(id+"F28.opExtrude","SWEPT_FACE",FACE,{"disambiguationData":[OSD([sQuery(id+"F11.wireOp",EDGE,"E30.top")])]});
            extrude(context, id + "F29", {"entities" : qUnion([Q0, Q1]), "operationType" : NewBodyOperationType.ADD, "endBound" : BoundingType.UP_TO_SURFACE, "oppositeDirection" : true, "endBoundEntityFace" : qUnion([Q2]), "depth" : 25 * mm});
        }
        {
            var Q0;
            Q0=makeQuery(id+"F1.opExtrude","CAP_FACE",FACE,{"disambiguationData":[OSD([sQuery(id+"F0.wireOp",EDGE,"E0.bottom"),sQuery(id+"F0.wireOp",EDGE,"E0.top"),sQuery(id+"F0.wireOp",EDGE,"E0.left"),sQuery(id+"F0.wireOp",EDGE,"E0.right"),sQuery(id+"F0.wireOp",EDGE,"E3")])],"isStart":true});
            var sketch = newSketch(context, id + "F30", { "sketchPlane" : qUnion([Q0])});
            skLineSegment(sketch, "E45.bottom", {"start": v(-945, 500) * mm, "end": v(-15, 500) * mm});
            skLineSegment(sketch, "E45.top", {"start": v(-945, -18.82) * mm, "end": v(-15, -18.82) * mm});
            skLineSegment(sketch, "E45.left", {"start": v(-945, 500) * mm, "end": v(-945, -18.82) * mm});
            skLineSegment(sketch, "E45.right", {"start": v(-15, 500) * mm, "end": v(-15, -18.82) * mm});
            skSolve(sketch);
        }
        {
            var Q0;
            {var subQ5=sQuery(id+"F30.wireOp",EDGE,"E45.bottom");Q0=makeQuery(id+"F30.imprint","IMPRINT",FACE,{"disambiguationData":[TD([[makeQuery(id+"F30.imprint","IMPRINT",EDGE,{"derivedFrom":subQ5}),1.0]])]});}
            extrude(context, id + "F31", {"entities" : qUnion([Q0]), "depth" : 2 * mm});
        }
        {
            var Q0;
            Q0=qCreatedBy(makeId("Top.planeOp"),FACE);
            var sketch = newSketch(context, id + "F32", { "sketchPlane" : qUnion([Q0])});
            skLineSegment(sketch, "E46.bottom", {"start": v(-435, -300) * mm, "end": v(-15, -300) * mm});
            skLineSegment(sketch, "E46.top", {"start": v(-435, 0) * mm, "end": v(-15, 0) * mm});
            skLineSegment(sketch, "E46.left", {"start": v(-435, -300) * mm, "end": v(-435, 0) * mm});
            skLineSegment(sketch, "E46.right", {"start": v(-15, -300) * mm, "end": v(-15, 0) * mm});
            skSolve(sketch);
        }
        {
            var Q0;
            Q0=makeQuery(id+"F32.imprint","IMPRINT",FACE,{"disambiguationData":[TD([[makeQuery(id+"F32.imprint","IMPRINT",EDGE,{"derivedFrom":sQuery(id+"F32.wireOp",EDGE,"E46.bottom")}),1.0]])]});
            extrude(context, id + "F33", {"entities" : qUnion([Q0]), "oppositeDirection" : true, "depth" : 1000 * mm});
        }
        {
            var Q0;
            Q0=makeQuery(id+"F33.opExtrude","SWEPT_FACE",FACE,{"disambiguationData":[OSD([sQuery(id+"F32.wireOp",EDGE,"E46.bottom")])]});
            shell(context, id + "F34", {"entities" : qUnion([Q0]), "thickness" : 15 * mm});
        }
        {
            var Q0;
            Q0=makeQuery(id+"F34.opShell","OFFSET_FACE",FACE,{"disambiguationData":[OSD([sQuery(id+"F32.wireOp",EDGE,"E46.left")])]});
            var sketch = newSketch(context, id + "F35", { "sketchPlane" : qUnion([Q0])});
            skLineSegment(sketch, "E47", {"start": v(-157.5, -15) * mm, "end": v(-157.5, -257.5) * mm, "construction": true});
            skPoint(sketch, "E48", {"position": v(-157.5, -742.5) * mm});
            skPoint(sketch, "E49", {"position": v(-157.5, -500) * mm});
            skPoint(sketch, "E50", {"position": v(-157.5, -257.5) * mm});
            skLineSegment(sketch, "E51.trimOffspring", {"start": v(-157.5, -500) * mm, "end": v(-157.5, -742.5) * mm, "construction": true});
            skPoint(sketch, "E52.orphan", {"position": v(-157.5, -985) * mm});
            skLineSegment(sketch, "E53", {"start": v(-157.5, -257.5) * mm, "end": v(-157.5, -500) * mm, "construction": true});
            skLineSegment(sketch, "E54", {"start": v(-157.5, -742.5) * mm, "end": v(-157.5, -985) * mm, "construction": true});
            skLineSegment(sketch, "E55.bottom", {"start": v(-300, -265) * mm, "end": v(-15, -265) * mm});
            skLineSegment(sketch, "E55.top", {"start": v(-300, -250) * mm, "end": v(-15, -250) * mm});
            skLineSegment(sketch, "E55.left", {"start": v(-300, -265) * mm, "end": v(-300, -250) * mm});
            skLineSegment(sketch, "E55.right", {"start": v(-15, -265) * mm, "end": v(-15, -250) * mm});
            skLineSegment(sketch, "E56.bottom", {"start": v(-300, -507.5) * mm, "end": v(-15, -507.5) * mm});
            skLineSegment(sketch, "E56.top", {"start": v(-300, -492.5) * mm, "end": v(-15, -492.5) * mm});
            skLineSegment(sketch, "E56.left", {"start": v(-300, -507.5) * mm, "end": v(-300, -492.5) * mm});
            skLineSegment(sketch, "E56.right", {"start": v(-15, -507.5) * mm, "end": v(-15, -492.5) * mm});
            skLineSegment(sketch, "E57.bottom", {"start": v(-300, -750) * mm, "end": v(-15, -750) * mm});
            skLineSegment(sketch, "E57.top", {"start": v(-300, -735) * mm, "end": v(-15, -735) * mm});
            skLineSegment(sketch, "E57.left", {"start": v(-300, -750) * mm, "end": v(-300, -735) * mm});
            skLineSegment(sketch, "E57.right", {"start": v(-15, -750) * mm, "end": v(-15, -735) * mm});
            skSolve(sketch);
        }
        {
            var Q0;
            Q0=makeQuery(id+"F35.imprint","IMPRINT",FACE,{"disambiguationData":[TD([[makeQuery(id+"F35.imprint","IMPRINT",EDGE,{"derivedFrom":sQuery(id+"F35.wireOp",EDGE,"E55.bottom")}),1.0]])]});
            var Q1;
            Q1=makeQuery(id+"F35.imprint","IMPRINT",FACE,{"disambiguationData":[TD([[makeQuery(id+"F35.imprint","IMPRINT",EDGE,{"derivedFrom":sQuery(id+"F35.wireOp",EDGE,"E56.bottom")}),1.0]])]});
            var Q2;
            Q2=makeQuery(id+"F35.imprint","IMPRINT",FACE,{"disambiguationData":[TD([[makeQuery(id+"F35.imprint","IMPRINT",EDGE,{"derivedFrom":sQuery(id+"F35.wireOp",EDGE,"E57.bottom")}),1.0]])]});
            var Q3;
            Q3=makeQuery(id+"F34.opShell","OFFSET_FACE",FACE,{"disambiguationData":[OSD([sQuery(id+"F32.wireOp",EDGE,"E46.right")])]});
            extrude(context, id + "F36", {"entities" : qUnion([Q0, Q1, Q2]), "operationType" : NewBodyOperationType.ADD, "endBound" : BoundingType.UP_TO_SURFACE, "endBoundEntityFace" : qUnion([Q3]), "depth" : 25 * mm});
        }
    });
